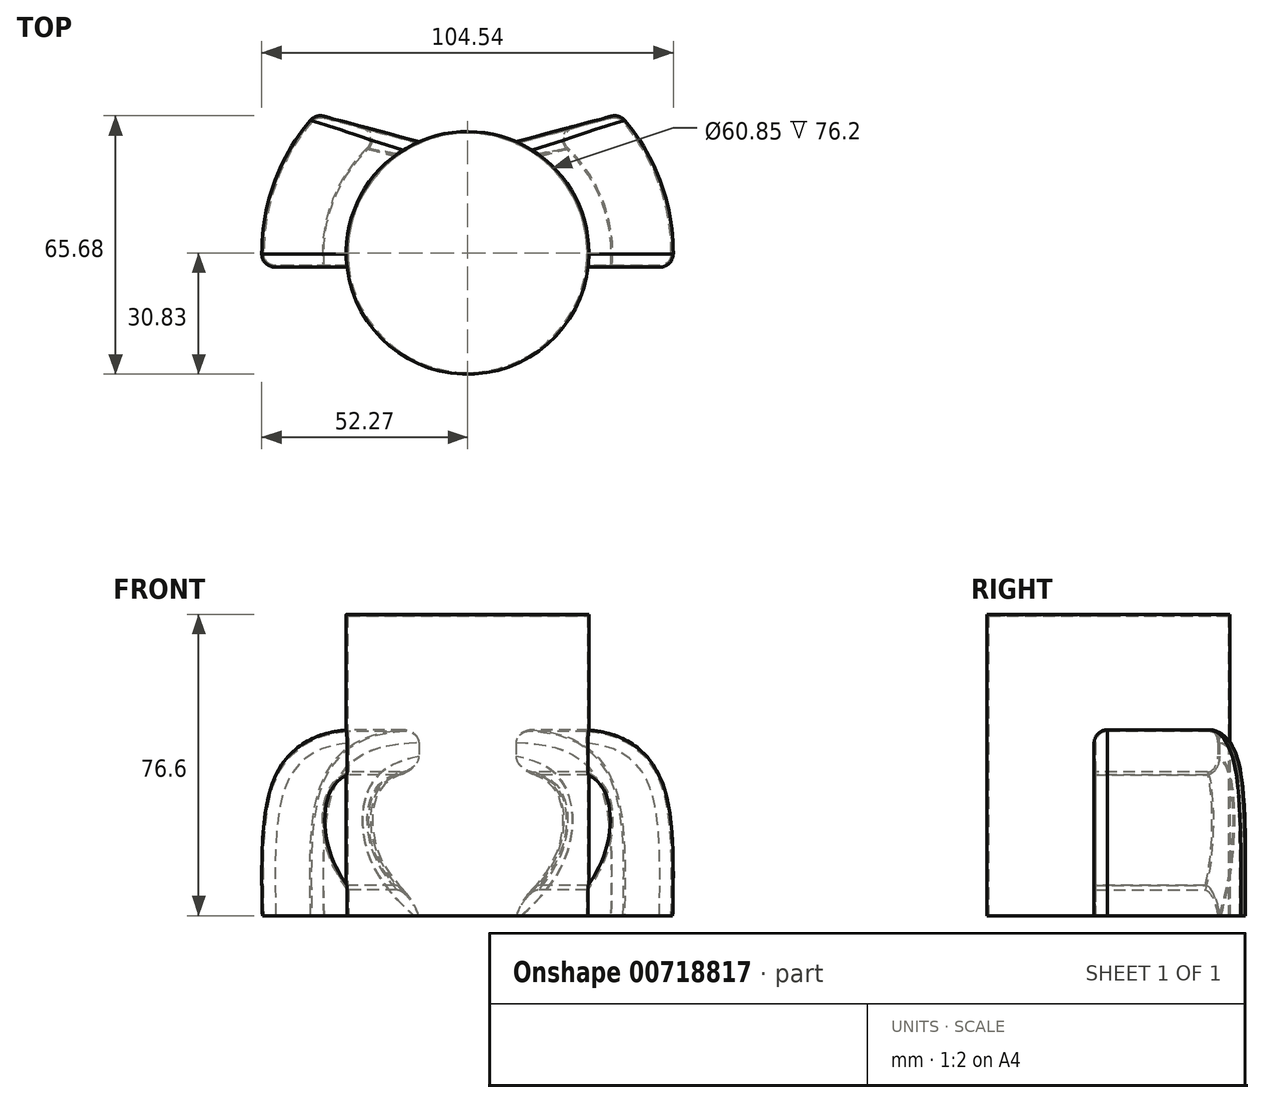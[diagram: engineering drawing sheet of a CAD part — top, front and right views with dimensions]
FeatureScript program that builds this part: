
annotation { "Feature Type Name" : "Feature", "Feature Type Description" : "" }
export const myFeature = defineFeature(function(context is Context, id is Id, definition is map)
    precondition{}
    {
        {
            var Q0;
            Q0=qCreatedBy(makeId("Front.planeOp"),FACE);
            var sketch = newSketch(context, id + "F0", { "sketchPlane" : qUnion([Q0])});
            skFitSpline(sketch, "E0", {"points": [v(-25.18, 0) * mm, v(-35.68, 16.54) * mm, v(-34.1, 33.77) * mm, v(-19.24, 38.82) * mm, v(0, 40.1) * mm], "startDerivative": vector(-48.95, 58.04) * mm, "endDerivative": vector(73.87, 3.97) * mm});
            skFitSpline(sketch, "E1", {"points": [v(-51.72, 0) * mm, v(-48.65, 34.86) * mm, v(-37.36, 45.45) * mm, v(-20.82, 47.14) * mm, v(0, 47.14) * mm], "startDerivative": vector(-2.54, 124.36) * mm, "endDerivative": vector(86.02, 0.14) * mm});
            skLineSegment(sketch, "E2", {"start": v(0, 60.11) * mm, "end": v(0, 0) * mm});
            skLineSegment(sketch, "E3", {"start": v(0, 0) * mm, "end": v(-59.15, 0) * mm});
            skSolve(sketch);
        }
        {
            var Q0;
            {var subQ0=sQuery(id+"F0.wireOp",EDGE,"E0");Q0=makeQuery(id+"F0.imprint","IMPRINT",FACE,{"disambiguationData":[TD([[makeQuery(id+"F0.imprint","IMPRINT",EDGE,{"derivedFrom":subQ0}),1.0]])]});}
            var Q1;
            Q1=sQuery(id+"F0.wireOp",EDGE,"E2");
            revolve(context, id + "F1", {"surfaceOperationType" : NewSurfaceOperationType.NEW, "entities" : qUnion([Q0]), "axis" : qUnion([Q1]), "revolveType" : RevolveType.FULL});
        }
        {
            var Q0;
            Q0=qCreatedBy(makeId("Top.planeOp"),FACE);
            var sketch = newSketch(context, id + "F2", { "sketchPlane" : qUnion([Q0])});
            skCircle(sketch, "E4", {"center": v(0, 0) * mm, "radius": 30.43 * mm});
            skSolve(sketch);
        }
        {
            var Q0;
            Q0=makeQuery(id+"F2.imprint","IMPRINT",FACE,{"disambiguationData":[TD([[makeQuery(id+"F2.imprint","IMPRINT",EDGE,{"derivedFrom":sQuery(id+"F2.wireOp",EDGE,"E4")}),1.0]])]});
            var Q1;
            Q1=sQuery(id+"F2.wireOp",EDGE,"E4");
            extrude(context, id + "F3", {"entities" : qUnion([Q0]), "surfaceEntities" : qUnion([Q1]), "depth" : 76.2 * mm, "offsetDistance" : 25.4 * mm});
        }
        {
            var Q0;
            Q0=qCreatedBy(makeId("Top.planeOp"),FACE);
            var sketch = newSketch(context, id + "F4", { "sketchPlane" : qUnion([Q0])});
            skLineSegment(sketch, "E5", {"start": v(-8.68, 26.86) * mm, "end": v(-38.28, 34.79) * mm});
            skLineSegment(sketch, "E6", {"start": v(-24.97, -3.24) * mm, "end": v(-51.62, -3.24) * mm});
            skLineSegment(sketch, "E7", {"start": v(-13.09, -21.51) * mm, "end": v(-37.5, -35.61) * mm});
            skLineSegment(sketch, "E8", {"start": v(-25.18, 0) * mm, "end": v(-51.72, 0) * mm});
            skArc(sketch, "E9", {"start": v(-6.1, 24.43) * mm, "mid": v(-7.09, 25.97) * mm, "end": v(-8.68, 26.86) * mm});
            skLineSegment(sketch, "E10", {"start": v(0, -55.04) * mm, "end": v(0, 57.97) * mm, "construction": true});
            skLineSegment(sketch, "E11.MirrorCS", {"start": v(13.09, -21.51) * mm, "end": v(37.5, -35.61) * mm});
            skLineSegment(sketch, "E12.MirrorCS", {"start": v(25.18, 0) * mm, "end": v(51.72, 0) * mm});
            skLineSegment(sketch, "E13.MirrorCS", {"start": v(24.97, -3.24) * mm, "end": v(51.62, -3.24) * mm});
            skLineSegment(sketch, "E14.MirrorCS", {"start": v(8.68, 26.86) * mm, "end": v(38.28, 34.79) * mm});
            skArc(sketch, "E15.MirrorCS", {"start": v(6.1, 24.43) * mm, "mid": v(7.09, 25.97) * mm, "end": v(8.68, 26.86) * mm});
            skLineSegment(sketch, "E16", {"start": v(-13.09, -21.51) * mm, "end": v(-26.84, -44.21) * mm});
            skLineSegment(sketch, "E17", {"start": v(-6.1, 24.43) * mm, "end": v(-14.44, 49.67) * mm});
            skLineSegment(sketch, "E18.MirrorCS", {"start": v(13.09, -21.51) * mm, "end": v(26.84, -44.21) * mm});
            skLineSegment(sketch, "E19.MirrorCS", {"start": v(6.1, 24.43) * mm, "end": v(14.44, 49.67) * mm});
            skSolve(sketch);
        }
        {
            var Q0;
            Q0=qCreatedBy(makeId("Top.planeOp"),FACE);
            var sketch = newSketch(context, id + "F5", { "sketchPlane" : qUnion([Q0])});
            skLineSegment(sketch, "E20.0", {"start": v(-6.1, 24.43) * mm, "end": v(-17.98, 60.38) * mm});
            skLineSegment(sketch, "E21.0", {"start": v(-13.09, -21.51) * mm, "end": v(-32.68, -53.86) * mm});
            skLineSegment(sketch, "E22.0", {"start": v(13.09, -21.51) * mm, "end": v(32.68, -53.86) * mm});
            skLineSegment(sketch, "E23.0", {"start": v(6.1, 24.43) * mm, "end": v(17.98, 60.38) * mm});
            skCircle(sketch, "E24.0.0", {"center": v(0, 0) * mm, "radius": 51.72 * mm});
            skLineSegment(sketch, "E25.0", {"start": v(-13.09, -21.51) * mm, "end": v(-47.5, -41.38) * mm});
            skLineSegment(sketch, "E26.0", {"start": v(-24.97, -3.24) * mm, "end": v(-62.91, -3.24) * mm});
            skLineSegment(sketch, "E27.0", {"start": v(-25.18, 0) * mm, "end": v(-63, 0) * mm});
            skLineSegment(sketch, "E28.0", {"start": v(-8.68, 26.86) * mm, "end": v(-50.25, 38) * mm});
            skArc(sketch, "E29.0", {"start": v(-6.1, 24.43) * mm, "mid": v(-7.09, 25.97) * mm, "end": v(-8.68, 26.86) * mm});
            skLineSegment(sketch, "E30.0", {"start": v(8.68, 26.86) * mm, "end": v(50.25, 38) * mm});
            skArc(sketch, "E31.0", {"start": v(6.1, 24.43) * mm, "mid": v(7.09, 25.97) * mm, "end": v(8.68, 26.86) * mm});
            skLineSegment(sketch, "E32.0", {"start": v(25.18, 0) * mm, "end": v(63, 0) * mm});
            skLineSegment(sketch, "E33.0", {"start": v(24.97, -3.24) * mm, "end": v(62.91, -3.24) * mm});
            skLineSegment(sketch, "E34.0", {"start": v(13.09, -21.51) * mm, "end": v(47.5, -41.38) * mm});
            skCircle(sketch, "E35.0", {"center": v(0, 0) * mm, "radius": 30.43 * mm});
            skCircle(sketch, "E36", {"center": v(0, 0) * mm, "radius": 63 * mm});
            skPoint(sketch, "E37.orphan", {"position": v(-14.44, 49.67) * mm});
            skPoint(sketch, "E38.orphan", {"position": v(14.44, 49.67) * mm});
            skPoint(sketch, "E39.orphan", {"position": v(38.28, 34.79) * mm});
            skPoint(sketch, "E40.orphan", {"position": v(51.72, 0) * mm});
            skPoint(sketch, "E41.orphan", {"position": v(51.62, -3.24) * mm});
            skPoint(sketch, "E42.orphan", {"position": v(37.5, -35.61) * mm});
            skPoint(sketch, "E43.orphan", {"position": v(26.84, -44.21) * mm});
            skPoint(sketch, "E44.orphan", {"position": v(-38.28, 34.79) * mm});
            skPoint(sketch, "E45.orphan", {"position": v(-51.72, 0) * mm});
            skPoint(sketch, "E46.orphan", {"position": v(-51.62, -3.24) * mm});
            skPoint(sketch, "E47.orphan", {"position": v(-37.5, -35.61) * mm});
            skPoint(sketch, "E48.orphan", {"position": v(-26.84, -44.21) * mm});
            skSolve(sketch);
        }
        {
            var Q0;
            {var subQ0=sQuery(id+"F5.wireOp",EDGE,"E35.0");var subQ1=sQuery(id+"F5.wireOp",EDGE,"E20.0");var subQ2=makeQuery(id+"F5.imprint","INTERSECT",VERTEX,{"derivedFrom":[subQ1,subQ0]});Q0=makeQuery(id+"F5.imprint","IMPRINT",FACE,{"disambiguationData":[TD([[makeQuery(id+"F5.imprint","IMPRINT",EDGE,{"disambiguationData":[TD([[subQ2,-1.0]])],"derivedFrom":subQ1}),1.0]])]});}
            var Q1;
            {var subQ0=sQuery(id+"F5.wireOp",EDGE,"E35.0");var subQ1=sQuery(id+"F5.wireOp",EDGE,"E20.0");var subQ2=makeQuery(id+"F5.imprint","INTERSECT",VERTEX,{"derivedFrom":[subQ1,subQ0]});Q1=makeQuery(id+"F5.imprint","IMPRINT",FACE,{"disambiguationData":[TD([[makeQuery(id+"F5.imprint","IMPRINT",EDGE,{"disambiguationData":[TD([[subQ2,-1.0]])],"derivedFrom":subQ1}),-1.0]])]});}
            var Q2;
            {var subQ0=sQuery(id+"F5.wireOp",EDGE,"E35.0");var subQ1=sQuery(id+"F5.wireOp",EDGE,"E23.0");var subQ2=makeQuery(id+"F5.imprint","INTERSECT",VERTEX,{"derivedFrom":[subQ1,subQ0]});Q2=makeQuery(id+"F5.imprint","IMPRINT",FACE,{"disambiguationData":[TD([[makeQuery(id+"F5.imprint","IMPRINT",EDGE,{"disambiguationData":[TD([[subQ2,-1.0]])],"derivedFrom":subQ1}),-1.0]])]});}
            var Q3;
            {var subQ0=sQuery(id+"F5.wireOp",EDGE,"E36");var subQ1=sQuery(id+"F5.wireOp",EDGE,"E23.0");var subQ2=makeQuery(id+"F5.imprint","INTERSECT",VERTEX,{"derivedFrom":[subQ1,subQ0]});Q3=makeQuery(id+"F5.imprint","IMPRINT",FACE,{"disambiguationData":[TD([[makeQuery(id+"F5.imprint","IMPRINT",EDGE,{"disambiguationData":[TD([[subQ2,1.0]])],"derivedFrom":subQ1}),-1.0]])]});}
            var Q4;
            {var subQ0=sQuery(id+"F5.wireOp",EDGE,"E36");var subQ1=sQuery(id+"F5.wireOp",EDGE,"E20.0");var subQ2=makeQuery(id+"F5.imprint","INTERSECT",VERTEX,{"derivedFrom":[subQ1,subQ0]});Q4=makeQuery(id+"F5.imprint","IMPRINT",FACE,{"disambiguationData":[TD([[makeQuery(id+"F5.imprint","IMPRINT",EDGE,{"disambiguationData":[TD([[subQ2,1.0]])],"derivedFrom":subQ1}),-1.0]])]});}
            var Q5;
            {var subQ0=sQuery(id+"F5.wireOp",EDGE,"E36");var subQ1=sQuery(id+"F5.wireOp",EDGE,"E20.0");var subQ2=makeQuery(id+"F5.imprint","INTERSECT",VERTEX,{"derivedFrom":[subQ1,subQ0]});Q5=makeQuery(id+"F5.imprint","IMPRINT",FACE,{"disambiguationData":[TD([[makeQuery(id+"F5.imprint","IMPRINT",EDGE,{"disambiguationData":[TD([[subQ2,1.0]])],"derivedFrom":subQ1}),1.0]])]});}
            var Q6;
            {var subQ0=sQuery(id+"F5.wireOp",EDGE,"E33.0");var subQ1=sQuery(id+"F5.wireOp",EDGE,"E24.0.0");var subQ2=makeQuery(id+"F5.imprint","INTERSECT",VERTEX,{"derivedFrom":[subQ1,subQ0]});Q6=makeQuery(id+"F5.imprint","IMPRINT",FACE,{"disambiguationData":[TD([[makeQuery(id+"F5.imprint","IMPRINT",EDGE,{"disambiguationData":[TD([[subQ2,1.0]])],"derivedFrom":subQ1}),-1.0]])]});}
            var Q7;
            {var subQ0=sQuery(id+"F5.wireOp",EDGE,"E33.0");var subQ1=sQuery(id+"F5.wireOp",EDGE,"E24.0.0");var subQ2=makeQuery(id+"F5.imprint","INTERSECT",VERTEX,{"derivedFrom":[subQ1,subQ0]});Q7=makeQuery(id+"F5.imprint","IMPRINT",FACE,{"disambiguationData":[TD([[makeQuery(id+"F5.imprint","IMPRINT",EDGE,{"disambiguationData":[TD([[subQ2,1.0]])],"derivedFrom":subQ1}),1.0]])]});}
            var Q8;
            {var subQ0=sQuery(id+"F5.wireOp",EDGE,"E26.0");var subQ1=sQuery(id+"F5.wireOp",EDGE,"E24.0.0");var subQ2=makeQuery(id+"F5.imprint","INTERSECT",VERTEX,{"derivedFrom":[subQ1,subQ0]});Q8=makeQuery(id+"F5.imprint","IMPRINT",FACE,{"disambiguationData":[TD([[makeQuery(id+"F5.imprint","IMPRINT",EDGE,{"disambiguationData":[TD([[subQ2,-1.0]])],"derivedFrom":subQ1}),-1.0]])]});}
            var Q9;
            {var subQ0=sQuery(id+"F5.wireOp",EDGE,"E26.0");var subQ1=sQuery(id+"F5.wireOp",EDGE,"E24.0.0");var subQ2=makeQuery(id+"F5.imprint","INTERSECT",VERTEX,{"derivedFrom":[subQ1,subQ0]});Q9=makeQuery(id+"F5.imprint","IMPRINT",FACE,{"disambiguationData":[TD([[makeQuery(id+"F5.imprint","IMPRINT",EDGE,{"disambiguationData":[TD([[subQ2,-1.0]])],"derivedFrom":subQ1}),1.0]])]});}
            var Q10;
            {var subQ0=sQuery(id+"F5.wireOp",EDGE,"E36");var subQ1=sQuery(id+"F5.wireOp",EDGE,"E22.0");var subQ2=makeQuery(id+"F5.imprint","INTERSECT",VERTEX,{"derivedFrom":[subQ1,subQ0]});Q10=makeQuery(id+"F5.imprint","IMPRINT",FACE,{"disambiguationData":[TD([[makeQuery(id+"F5.imprint","IMPRINT",EDGE,{"disambiguationData":[TD([[subQ2,1.0]])],"derivedFrom":subQ1}),1.0]])]});}
            var Q11;
            {var subQ0=sQuery(id+"F5.wireOp",EDGE,"E35.0");var subQ1=sQuery(id+"F5.wireOp",EDGE,"E22.0");var subQ2=makeQuery(id+"F5.imprint","INTERSECT",VERTEX,{"derivedFrom":[subQ1,subQ0]});Q11=makeQuery(id+"F5.imprint","IMPRINT",FACE,{"disambiguationData":[TD([[makeQuery(id+"F5.imprint","IMPRINT",EDGE,{"disambiguationData":[TD([[subQ2,-1.0]])],"derivedFrom":subQ1}),1.0]])]});}
            var Q12;
            {var subQ0=sQuery(id+"F5.wireOp",EDGE,"E36");var subQ1=sQuery(id+"F5.wireOp",EDGE,"E21.0");var subQ2=makeQuery(id+"F5.imprint","INTERSECT",VERTEX,{"derivedFrom":[subQ1,subQ0]});Q12=makeQuery(id+"F5.imprint","IMPRINT",FACE,{"disambiguationData":[TD([[makeQuery(id+"F5.imprint","IMPRINT",EDGE,{"disambiguationData":[TD([[subQ2,1.0]])],"derivedFrom":subQ1}),-1.0]])]});}
            var Q13;
            {var subQ0=sQuery(id+"F5.wireOp",EDGE,"E35.0");var subQ1=sQuery(id+"F5.wireOp",EDGE,"E21.0");var subQ2=makeQuery(id+"F5.imprint","INTERSECT",VERTEX,{"derivedFrom":[subQ1,subQ0]});Q13=makeQuery(id+"F5.imprint","IMPRINT",FACE,{"disambiguationData":[TD([[makeQuery(id+"F5.imprint","IMPRINT",EDGE,{"disambiguationData":[TD([[subQ2,-1.0]])],"derivedFrom":subQ1}),-1.0]])]});}
            var Q14;
            {var subQ0=sQuery(id+"F5.wireOp",EDGE,"E35.0");var subQ1=sQuery(id+"F5.wireOp",EDGE,"E21.0");var subQ2=makeQuery(id+"F5.imprint","INTERSECT",VERTEX,{"derivedFrom":[subQ1,subQ0]});Q14=makeQuery(id+"F5.imprint","IMPRINT",FACE,{"disambiguationData":[TD([[makeQuery(id+"F5.imprint","IMPRINT",EDGE,{"disambiguationData":[TD([[subQ2,-1.0]])],"derivedFrom":subQ1}),1.0]])]});}
            var Q15;
            {var subQ0=sQuery(id+"F5.wireOp",EDGE,"E36");var subQ1=sQuery(id+"F5.wireOp",EDGE,"E21.0");var subQ2=makeQuery(id+"F5.imprint","INTERSECT",VERTEX,{"derivedFrom":[subQ1,subQ0]});Q15=makeQuery(id+"F5.imprint","IMPRINT",FACE,{"disambiguationData":[TD([[makeQuery(id+"F5.imprint","IMPRINT",EDGE,{"disambiguationData":[TD([[subQ2,1.0]])],"derivedFrom":subQ1}),1.0]])]});}
            extrude(context, id + "F6", {"entities" : qUnion([Q0, Q1, Q2, Q3, Q4, Q5, Q6, Q7, Q8, Q9, Q10, Q11, Q12, Q13, Q14, Q15]), "depth" : 76.2 * mm, "offsetDistance" : 25.4 * mm});
        }
        {
            var Q0;
            Q0=makeQuery(id+"F6.opExtrude","SWEPT_BODY",BODY,{"disambiguationData":[OSD([sQuery(id+"F5.wireOp",EDGE,"E28.0"),sQuery(id+"F5.wireOp",EDGE,"E30.0"),sQuery(id+"F5.wireOp",EDGE,"E35.0"),sQuery(id+"F5.wireOp",EDGE,"E36")])]});
            var Q1;
            Q1=makeQuery(id+"F6.opExtrude","SWEPT_BODY",BODY,{"disambiguationData":[OSD([sQuery(id+"F5.wireOp",EDGE,"E25.0"),sQuery(id+"F5.wireOp",EDGE,"E34.0"),sQuery(id+"F5.wireOp",EDGE,"E35.0"),sQuery(id+"F5.wireOp",EDGE,"E36")])]});
            var Q2;
            Q2=makeQuery(id+"F6.opExtrude","SWEPT_BODY",BODY,{"disambiguationData":[OSD([sQuery(id+"F5.wireOp",EDGE,"E26.0"),sQuery(id+"F5.wireOp",EDGE,"E27.0"),sQuery(id+"F5.wireOp",EDGE,"E35.0"),sQuery(id+"F5.wireOp",EDGE,"E36")])]});
            var Q3;
            Q3=makeQuery(id+"F6.opExtrude","SWEPT_BODY",BODY,{"disambiguationData":[OSD([sQuery(id+"F5.wireOp",EDGE,"E32.0"),sQuery(id+"F5.wireOp",EDGE,"E33.0"),sQuery(id+"F5.wireOp",EDGE,"E35.0"),sQuery(id+"F5.wireOp",EDGE,"E36")])]});
            var Q4;
            Q4=makeQuery(id+"F1.opRevolve","SWEPT_BODY",BODY,{"disambiguationData":[OSD([sQuery(id+"F0.wireOp",EDGE,"E0"),sQuery(id+"F0.wireOp",EDGE,"E1"),sQuery(id+"F0.wireOp",EDGE,"E2"),sQuery(id+"F0.wireOp",EDGE,"E3")])]});
            booleanBodies(context, id + "F7", {"operationType" : BooleanOperationType.SUBTRACTION, "tools" : qUnion([Q0, Q1, Q2, Q3]), "targets" : qUnion([Q4])});
        }
        {
            var Q0;
            Q0=makeQuery(id+"F7.opBoolean","INTERSECT",EDGE,{"derivedFrom":[makeQuery(id+"F1.opRevolve","SWEPT_FACE",FACE,{"disambiguationData":[OSD([sQuery(id+"F0.wireOp",EDGE,"E1")])]}),makeQuery(id+"F6.opExtrude","SWEPT_FACE",FACE,{"disambiguationData":[OSD([sQuery(id+"F5.wireOp",EDGE,"E28.0")])]})]});
            var Q1;
            Q1=makeQuery(id+"F7.opBoolean","INTERSECT",EDGE,{"derivedFrom":[makeQuery(id+"F1.opRevolve","SWEPT_FACE",FACE,{"disambiguationData":[OSD([sQuery(id+"F0.wireOp",EDGE,"E0")])]}),makeQuery(id+"F6.opExtrude","SWEPT_FACE",FACE,{"disambiguationData":[OSD([sQuery(id+"F5.wireOp",EDGE,"E30.0")])]})]});
            var Q2;
            Q2=makeQuery(id+"F7.opBoolean","INTERSECT",EDGE,{"derivedFrom":[makeQuery(id+"F1.opRevolve","SWEPT_FACE",FACE,{"disambiguationData":[OSD([sQuery(id+"F0.wireOp",EDGE,"E0")])]}),makeQuery(id+"F6.opExtrude","SWEPT_FACE",FACE,{"disambiguationData":[OSD([sQuery(id+"F5.wireOp",EDGE,"E28.0")])]})]});
            var Q3;
            Q3=makeQuery(id+"F7.opBoolean","INTERSECT",EDGE,{"derivedFrom":[makeQuery(id+"F1.opRevolve","SWEPT_FACE",FACE,{"disambiguationData":[OSD([sQuery(id+"F0.wireOp",EDGE,"E1")])]}),makeQuery(id+"F6.opExtrude","SWEPT_FACE",FACE,{"disambiguationData":[OSD([sQuery(id+"F5.wireOp",EDGE,"E30.0")])]})]});
            var Q4;
            Q4=makeQuery(id+"F7.opBoolean","INTERSECT",EDGE,{"derivedFrom":[makeQuery(id+"F1.opRevolve","SWEPT_FACE",FACE,{"disambiguationData":[OSD([sQuery(id+"F0.wireOp",EDGE,"E1")])]}),makeQuery(id+"F6.opExtrude","SWEPT_FACE",FACE,{"disambiguationData":[OSD([sQuery(id+"F5.wireOp",EDGE,"E32.0")])]})]});
            var Q5;
            Q5=makeQuery(id+"F7.opBoolean","INTERSECT",EDGE,{"derivedFrom":[makeQuery(id+"F1.opRevolve","SWEPT_FACE",FACE,{"disambiguationData":[OSD([sQuery(id+"F0.wireOp",EDGE,"E1")])]}),makeQuery(id+"F6.opExtrude","SWEPT_FACE",FACE,{"disambiguationData":[OSD([sQuery(id+"F5.wireOp",EDGE,"E33.0")])]})]});
            var Q6;
            Q6=makeQuery(id+"F7.opBoolean","INTERSECT",EDGE,{"derivedFrom":[makeQuery(id+"F1.opRevolve","SWEPT_FACE",FACE,{"disambiguationData":[OSD([sQuery(id+"F0.wireOp",EDGE,"E1")])]}),makeQuery(id+"F6.opExtrude","SWEPT_FACE",FACE,{"disambiguationData":[OSD([sQuery(id+"F5.wireOp",EDGE,"E34.0")])]})]});
            var Q7;
            Q7=makeQuery(id+"F7.opBoolean","INTERSECT",EDGE,{"derivedFrom":[makeQuery(id+"F1.opRevolve","SWEPT_FACE",FACE,{"disambiguationData":[OSD([sQuery(id+"F0.wireOp",EDGE,"E0")])]}),makeQuery(id+"F6.opExtrude","SWEPT_FACE",FACE,{"disambiguationData":[OSD([sQuery(id+"F5.wireOp",EDGE,"E32.0")])]})]});
            var Q8;
            Q8=makeQuery(id+"F7.opBoolean","INTERSECT",EDGE,{"derivedFrom":[makeQuery(id+"F1.opRevolve","SWEPT_FACE",FACE,{"disambiguationData":[OSD([sQuery(id+"F0.wireOp",EDGE,"E0")])]}),makeQuery(id+"F6.opExtrude","SWEPT_FACE",FACE,{"disambiguationData":[OSD([sQuery(id+"F5.wireOp",EDGE,"E34.0")])]})]});
            var Q9;
            Q9=makeQuery(id+"F7.opBoolean","INTERSECT",EDGE,{"derivedFrom":[makeQuery(id+"F1.opRevolve","SWEPT_FACE",FACE,{"disambiguationData":[OSD([sQuery(id+"F0.wireOp",EDGE,"E1")])]}),makeQuery(id+"F6.opExtrude","SWEPT_FACE",FACE,{"disambiguationData":[OSD([sQuery(id+"F5.wireOp",EDGE,"E25.0")])]})]});
            var Q10;
            Q10=makeQuery(id+"F7.opBoolean","INTERSECT",EDGE,{"derivedFrom":[makeQuery(id+"F1.opRevolve","SWEPT_FACE",FACE,{"disambiguationData":[OSD([sQuery(id+"F0.wireOp",EDGE,"E0")])]}),makeQuery(id+"F6.opExtrude","SWEPT_FACE",FACE,{"disambiguationData":[OSD([sQuery(id+"F5.wireOp",EDGE,"E25.0")])]})]});
            var Q11;
            Q11=makeQuery(id+"F7.opBoolean","INTERSECT",EDGE,{"derivedFrom":[makeQuery(id+"F1.opRevolve","SWEPT_FACE",FACE,{"disambiguationData":[OSD([sQuery(id+"F0.wireOp",EDGE,"E1")])]}),makeQuery(id+"F6.opExtrude","SWEPT_FACE",FACE,{"disambiguationData":[OSD([sQuery(id+"F5.wireOp",EDGE,"E27.0")])]})]});
            var Q12;
            Q12=makeQuery(id+"F7.opBoolean","INTERSECT",EDGE,{"derivedFrom":[makeQuery(id+"F1.opRevolve","SWEPT_FACE",FACE,{"disambiguationData":[OSD([sQuery(id+"F0.wireOp",EDGE,"E1")])]}),makeQuery(id+"F6.opExtrude","SWEPT_FACE",FACE,{"disambiguationData":[OSD([sQuery(id+"F5.wireOp",EDGE,"E26.0")])]})]});
            fillet(context, id + "F8", {"entities" : qUnion([Q0, Q1, Q2, Q3, Q4, Q5, Q6, Q7, Q8, Q9, Q10, Q11, Q12]), "radius" : 3 * mm, "tangentPropagation" : true, "allowEdgeOverflow" : false});
        }
        {
            var Q0;
            Q0=makeQuery(id+"F3.opExtrude","SWEPT_BODY",BODY,{"disambiguationData":[OSD([sQuery(id+"F2.wireOp",EDGE,"E4")])]});
            var Q1;
            Q1=makeQuery(id+"F1.opRevolve","SWEPT_BODY",BODY,{"disambiguationData":[OSD([sQuery(id+"F0.wireOp",EDGE,"E0"),sQuery(id+"F0.wireOp",EDGE,"E1"),sQuery(id+"F0.wireOp",EDGE,"E2"),sQuery(id+"F0.wireOp",EDGE,"E3")])]});
            booleanBodies(context, id + "F9", {"operationType" : BooleanOperationType.UNION, "tools" : qUnion([Q0, Q1])});
        }
        {
            var Q0;
            Q0=makeQuery(id+"F9.opBoolean","MERGE",FACE,{"derivedFrom":[makeQuery(id+"F3.opExtrude","CAP_FACE",FACE,{"disambiguationData":[OSD([sQuery(id+"F2.wireOp",EDGE,"E4")])],"isStart":true}),makeQuery(id+"F1.opRevolve","SWEPT_FACE",FACE,{"disambiguationData":[OSD([sQuery(id+"F0.wireOp",EDGE,"E3")])]})]});
            shell(context, id + "F10", {"entities" : qUnion([Q0]), "thickness" : 0.4 * mm, "oppositeDirection" : true});
        }
    });
